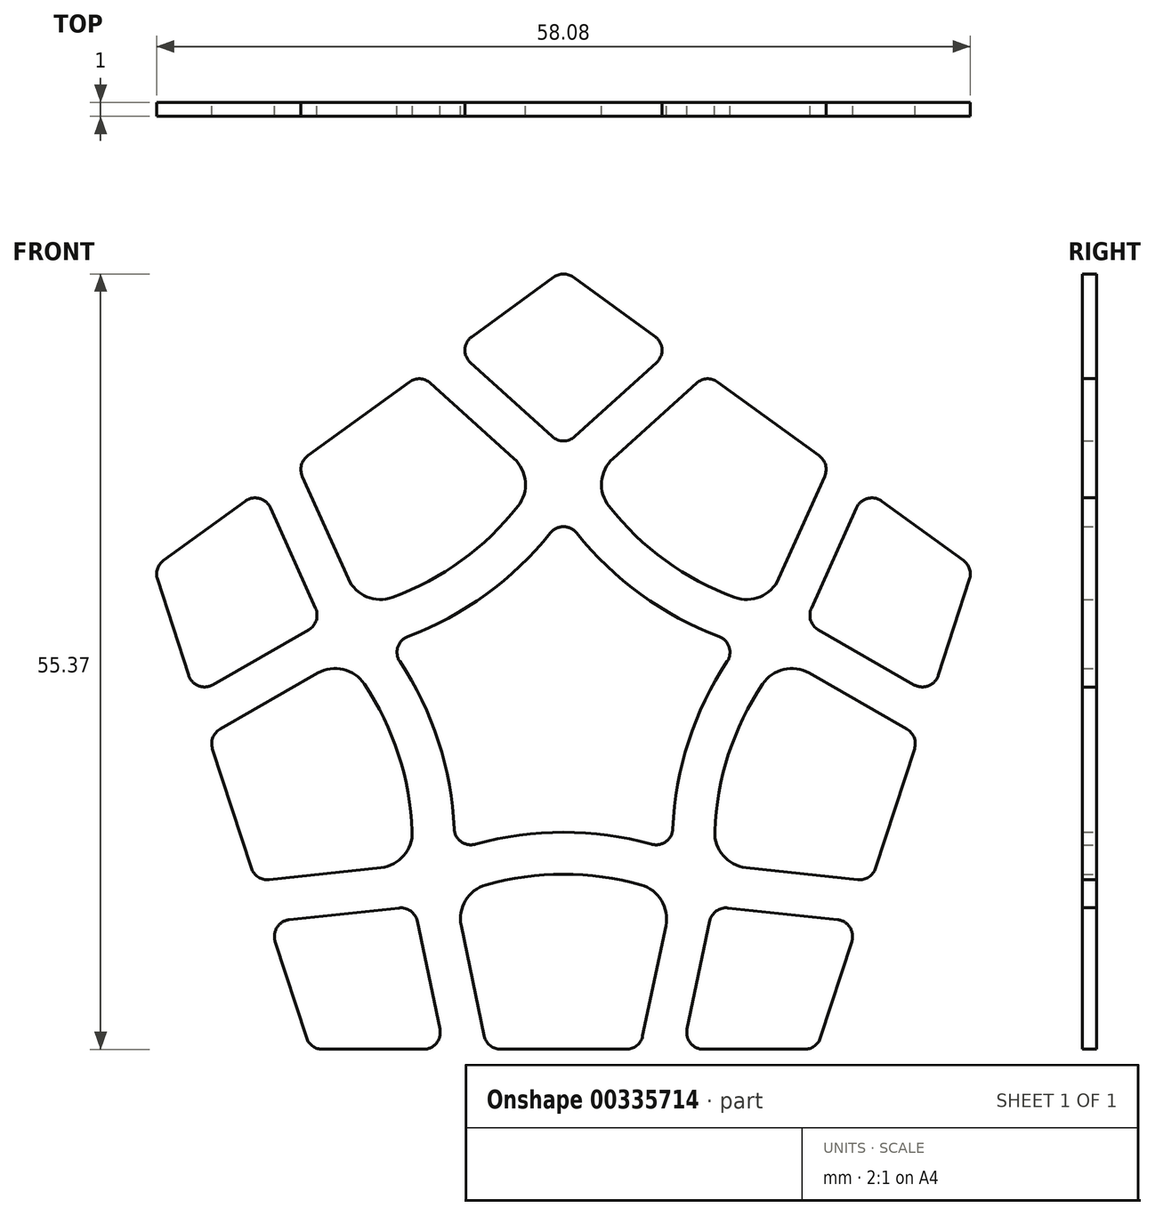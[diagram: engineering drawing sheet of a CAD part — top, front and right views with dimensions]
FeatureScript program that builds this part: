
annotation { "Feature Type Name" : "Feature", "Feature Type Description" : "" }
export const myFeature = defineFeature(function(context is Context, id is Id, definition is map)
    precondition{}
    {
        {
            var Q0;
            Q0=qCreatedBy(makeId("Front.planeOp"),FACE);
            var sketch = newSketch(context, id + "F0", { "sketchPlane" : qUnion([Q0])});
            skCircle(sketch, "E0.cCircle", {"center": v(0, 0) * mm, "radius": 26.39 * mm, "construction": true});
            skLineSegment(sketch, "E0.0", {"start": v(19.17, -26.39) * mm, "end": v(-19.17, -26.39) * mm});
            skLineSegment(sketch, "E0.1", {"start": v(-19.17, -26.39) * mm, "end": v(-31.02, 10.08) * mm});
            skLineSegment(sketch, "E0.2", {"start": v(-31.02, 10.08) * mm, "end": v(0, 32.61) * mm});
            skLineSegment(sketch, "E0.3", {"start": v(0, 32.61) * mm, "end": v(31.02, 10.08) * mm});
            skLineSegment(sketch, "E0.4", {"start": v(31.02, 10.08) * mm, "end": v(19.17, -26.39) * mm});
            skPoint(sketch, "E0.0.midPoint", {"position": v(0, -26.39) * mm});
            skArc(sketch, "E1", {"start": v(9.47, -13.04) * mm, "mid": v(0, -10.89) * mm, "end": v(-9.47, -13.04) * mm, "construction": true});
            skLineSegment(sketch, "E2", {"start": v(-19.57, -15.63) * mm, "end": v(-11.74, -14.79) * mm});
            skLineSegment(sketch, "E3", {"start": v(-10.44, -15.74) * mm, "end": v(-8.82, -23.44) * mm});
            skLineSegment(sketch, "E4", {"start": v(-10, -24.89) * mm, "end": v(-17.2, -24.89) * mm});
            skLineSegment(sketch, "E5", {"start": v(-18.35, -24.06) * mm, "end": v(-20.58, -17.2) * mm});
            skPoint(sketch, "E6.visualSharp", {"position": v(-21.04, -15.8) * mm});
            skArc(sketch, "E6.filletArc", {"start": v(-19.57, -15.63) * mm, "mid": v(-20.44, -16.17) * mm, "end": v(-20.58, -17.2) * mm});
            skPoint(sketch, "E7.visualSharp", {"position": v(-10.66, -14.67) * mm});
            skArc(sketch, "E7.filletArc", {"start": v(-10.44, -15.74) * mm, "mid": v(-10.9, -15.01) * mm, "end": v(-11.74, -14.79) * mm});
            skPoint(sketch, "E8.visualSharp", {"position": v(-8.52, -24.89) * mm});
            skArc(sketch, "E8.filletArc", {"start": v(-10, -24.89) * mm, "mid": v(-9.06, -24.44) * mm, "end": v(-8.82, -23.44) * mm});
            skPoint(sketch, "E9.visualSharp", {"position": v(-18.08, -24.89) * mm});
            skArc(sketch, "E9.filletArc", {"start": v(-18.35, -24.06) * mm, "mid": v(-17.91, -24.66) * mm, "end": v(-17.2, -24.89) * mm});
            skLineSegment(sketch, "E10", {"start": v(-7.3, -16.07) * mm, "end": v(-5.65, -23.93) * mm});
            skLineSegment(sketch, "E11", {"start": v(-4.48, -24.89) * mm, "end": v(4.48, -24.89) * mm});
            skLineSegment(sketch, "E12", {"start": v(5.65, -23.93) * mm, "end": v(7.3, -16.07) * mm});
            skArc(sketch, "E13", {"start": v(5.53, -13.15) * mm, "mid": v(0, -12.39) * mm, "end": v(-5.53, -13.15) * mm});
            skPoint(sketch, "E14.visualSharp", {"position": v(-5.45, -24.89) * mm});
            skArc(sketch, "E14.filletArc", {"start": v(-5.65, -23.93) * mm, "mid": v(-5.23, -24.62) * mm, "end": v(-4.48, -24.89) * mm});
            skPoint(sketch, "E15.visualSharp", {"position": v(5.45, -24.89) * mm});
            skArc(sketch, "E15.filletArc", {"start": v(4.48, -24.89) * mm, "mid": v(5.23, -24.62) * mm, "end": v(5.65, -23.93) * mm});
            skPoint(sketch, "E16.visualSharp", {"position": v(-7.75, -13.91) * mm});
            skArc(sketch, "E16.filletArc", {"start": v(-5.53, -13.15) * mm, "mid": v(-7, -14.26) * mm, "end": v(-7.3, -16.07) * mm});
            skPoint(sketch, "E17.visualSharp", {"position": v(7.75, -13.91) * mm});
            skArc(sketch, "E17.filletArc", {"start": v(7.3, -16.07) * mm, "mid": v(7, -14.26) * mm, "end": v(5.53, -13.15) * mm});
            skLineSegment(sketch, "E18.1.0", {"start": v(8.82, -23.44) * mm, "end": v(10.44, -15.74) * mm});
            skArc(sketch, "E18.1.1", {"start": v(8.82, -23.44) * mm, "mid": v(9.06, -24.44) * mm, "end": v(10, -24.89) * mm});
            skLineSegment(sketch, "E18.1.2", {"start": v(17.2, -24.89) * mm, "end": v(10, -24.89) * mm});
            skArc(sketch, "E18.1.3", {"start": v(17.2, -24.89) * mm, "mid": v(17.91, -24.66) * mm, "end": v(18.35, -24.06) * mm});
            skLineSegment(sketch, "E18.1.4", {"start": v(20.58, -17.2) * mm, "end": v(18.35, -24.06) * mm});
            skArc(sketch, "E18.1.5", {"start": v(20.58, -17.2) * mm, "mid": v(20.44, -16.17) * mm, "end": v(19.57, -15.63) * mm});
            skLineSegment(sketch, "E18.1.6", {"start": v(11.74, -14.79) * mm, "end": v(19.57, -15.63) * mm});
            skArc(sketch, "E18.1.7", {"start": v(11.74, -14.79) * mm, "mid": v(10.9, -15.01) * mm, "end": v(10.44, -15.74) * mm});
            skArc(sketch, "E18.1.8", {"start": v(10.8, -9.33) * mm, "mid": v(11.4, -11.06) * mm, "end": v(13.03, -11.91) * mm});
            skLineSegment(sketch, "E18.1.9", {"start": v(13.03, -11.91) * mm, "end": v(21.01, -12.77) * mm});
            skArc(sketch, "E18.1.10", {"start": v(21.01, -12.77) * mm, "mid": v(21.8, -12.59) * mm, "end": v(22.28, -11.95) * mm});
            skLineSegment(sketch, "E18.1.11", {"start": v(22.28, -11.95) * mm, "end": v(25.05, -3.43) * mm});
            skArc(sketch, "E18.1.12", {"start": v(25.05, -3.43) * mm, "mid": v(25.03, -2.63) * mm, "end": v(24.5, -2.02) * mm});
            skLineSegment(sketch, "E18.1.13", {"start": v(24.5, -2.02) * mm, "end": v(17.54, 1.98) * mm});
            skArc(sketch, "E18.1.14", {"start": v(17.54, 1.98) * mm, "mid": v(15.72, 2.25) * mm, "end": v(14.22, 1.2) * mm});
            skArc(sketch, "E18.1.15", {"start": v(14.22, 1.2) * mm, "mid": v(11.78, -3.83) * mm, "end": v(10.8, -9.33) * mm});
            skLineSegment(sketch, "E18.2.0", {"start": v(25.02, 1.15) * mm, "end": v(18.2, 5.06) * mm});
            skArc(sketch, "E18.2.1", {"start": v(25.02, 1.15) * mm, "mid": v(26.05, 1.07) * mm, "end": v(26.76, 1.82) * mm});
            skLineSegment(sketch, "E18.2.2", {"start": v(28.99, 8.68) * mm, "end": v(26.76, 1.82) * mm});
            skArc(sketch, "E18.2.3", {"start": v(28.99, 8.68) * mm, "mid": v(28.99, 9.42) * mm, "end": v(28.55, 10.02) * mm});
            skLineSegment(sketch, "E18.2.4", {"start": v(22.71, 14.26) * mm, "end": v(28.55, 10.02) * mm});
            skArc(sketch, "E18.2.5", {"start": v(22.71, 14.26) * mm, "mid": v(21.7, 14.45) * mm, "end": v(20.91, 13.78) * mm});
            skLineSegment(sketch, "E18.2.6", {"start": v(17.7, 6.6) * mm, "end": v(20.91, 13.78) * mm});
            skArc(sketch, "E18.2.7", {"start": v(17.7, 6.6) * mm, "mid": v(17.65, 5.73) * mm, "end": v(18.2, 5.06) * mm});
            skArc(sketch, "E18.2.8", {"start": v(12.2, 7.39) * mm, "mid": v(14.04, 7.43) * mm, "end": v(15.35, 8.7) * mm});
            skLineSegment(sketch, "E18.2.9", {"start": v(15.35, 8.7) * mm, "end": v(18.64, 16.04) * mm});
            skArc(sketch, "E18.2.10", {"start": v(18.64, 16.04) * mm, "mid": v(18.7, 16.84) * mm, "end": v(18.25, 17.5) * mm});
            skLineSegment(sketch, "E18.2.11", {"start": v(18.25, 17.5) * mm, "end": v(11, 22.77) * mm});
            skArc(sketch, "E18.2.12", {"start": v(11, 22.77) * mm, "mid": v(10.23, 23) * mm, "end": v(9.5, 22.68) * mm});
            skLineSegment(sketch, "E18.2.13", {"start": v(9.5, 22.68) * mm, "end": v(3.54, 17.3) * mm});
            skArc(sketch, "E18.2.14", {"start": v(3.54, 17.3) * mm, "mid": v(2.72, 15.65) * mm, "end": v(3.25, 13.9) * mm});
            skArc(sketch, "E18.2.15", {"start": v(3.25, 13.9) * mm, "mid": v(7.28, 10.02) * mm, "end": v(12.2, 7.39) * mm});
            skLineSegment(sketch, "E18.3.0", {"start": v(6.64, 24.15) * mm, "end": v(0.8, 18.87) * mm});
            skArc(sketch, "E18.3.1", {"start": v(6.64, 24.15) * mm, "mid": v(7.03, 25.1) * mm, "end": v(6.54, 26) * mm});
            skLineSegment(sketch, "E18.3.2", {"start": v(0.7, 30.25) * mm, "end": v(6.54, 26) * mm});
            skArc(sketch, "E18.3.3", {"start": v(0.7, 30.25) * mm, "mid": v(0, 30.48) * mm, "end": v(-0.7, 30.25) * mm});
            skLineSegment(sketch, "E18.3.4", {"start": v(-6.54, 26) * mm, "end": v(-0.7, 30.25) * mm});
            skArc(sketch, "E18.3.5", {"start": v(-6.54, 26) * mm, "mid": v(-7.03, 25.1) * mm, "end": v(-6.64, 24.15) * mm});
            skLineSegment(sketch, "E18.3.6", {"start": v(-0.8, 18.87) * mm, "end": v(-6.64, 24.15) * mm});
            skArc(sketch, "E18.3.7", {"start": v(-0.8, 18.87) * mm, "mid": v(0, 18.56) * mm, "end": v(0.8, 18.87) * mm});
            skArc(sketch, "E18.3.8", {"start": v(-3.25, 13.9) * mm, "mid": v(-2.72, 15.65) * mm, "end": v(-3.54, 17.3) * mm});
            skLineSegment(sketch, "E18.3.9", {"start": v(-3.54, 17.3) * mm, "end": v(-9.5, 22.68) * mm});
            skArc(sketch, "E18.3.10", {"start": v(-9.5, 22.68) * mm, "mid": v(-10.23, 23) * mm, "end": v(-11, 22.77) * mm});
            skLineSegment(sketch, "E18.3.11", {"start": v(-11, 22.77) * mm, "end": v(-18.25, 17.5) * mm});
            skArc(sketch, "E18.3.12", {"start": v(-18.25, 17.5) * mm, "mid": v(-18.7, 16.84) * mm, "end": v(-18.64, 16.04) * mm});
            skLineSegment(sketch, "E18.3.13", {"start": v(-18.64, 16.04) * mm, "end": v(-15.35, 8.7) * mm});
            skArc(sketch, "E18.3.14", {"start": v(-15.35, 8.7) * mm, "mid": v(-14.04, 7.43) * mm, "end": v(-12.2, 7.39) * mm});
            skArc(sketch, "E18.3.15", {"start": v(-12.2, 7.39) * mm, "mid": v(-7.28, 10.02) * mm, "end": v(-3.25, 13.9) * mm});
            skLineSegment(sketch, "E18.4.0", {"start": v(-20.91, 13.78) * mm, "end": v(-17.7, 6.6) * mm});
            skArc(sketch, "E18.4.1", {"start": v(-20.91, 13.78) * mm, "mid": v(-21.7, 14.45) * mm, "end": v(-22.71, 14.26) * mm});
            skLineSegment(sketch, "E18.4.2", {"start": v(-28.55, 10.02) * mm, "end": v(-22.71, 14.26) * mm});
            skArc(sketch, "E18.4.3", {"start": v(-28.55, 10.02) * mm, "mid": v(-28.99, 9.42) * mm, "end": v(-28.99, 8.68) * mm});
            skLineSegment(sketch, "E18.4.4", {"start": v(-26.76, 1.82) * mm, "end": v(-28.99, 8.68) * mm});
            skArc(sketch, "E18.4.5", {"start": v(-26.76, 1.82) * mm, "mid": v(-26.05, 1.07) * mm, "end": v(-25.02, 1.15) * mm});
            skLineSegment(sketch, "E18.4.6", {"start": v(-18.2, 5.06) * mm, "end": v(-25.02, 1.15) * mm});
            skArc(sketch, "E18.4.7", {"start": v(-18.2, 5.06) * mm, "mid": v(-17.65, 5.73) * mm, "end": v(-17.7, 6.6) * mm});
            skArc(sketch, "E18.4.8", {"start": v(-14.22, 1.2) * mm, "mid": v(-15.72, 2.25) * mm, "end": v(-17.54, 1.98) * mm});
            skLineSegment(sketch, "E18.4.9", {"start": v(-17.54, 1.98) * mm, "end": v(-24.5, -2.02) * mm});
            skArc(sketch, "E18.4.10", {"start": v(-24.5, -2.02) * mm, "mid": v(-25.03, -2.63) * mm, "end": v(-25.05, -3.43) * mm});
            skLineSegment(sketch, "E18.4.11", {"start": v(-25.05, -3.43) * mm, "end": v(-22.28, -11.95) * mm});
            skArc(sketch, "E18.4.12", {"start": v(-22.28, -11.95) * mm, "mid": v(-21.8, -12.59) * mm, "end": v(-21.01, -12.77) * mm});
            skLineSegment(sketch, "E18.4.13", {"start": v(-21.01, -12.77) * mm, "end": v(-13.03, -11.91) * mm});
            skArc(sketch, "E18.4.14", {"start": v(-13.03, -11.91) * mm, "mid": v(-11.4, -11.06) * mm, "end": v(-10.8, -9.33) * mm});
            skArc(sketch, "E18.4.15", {"start": v(-10.8, -9.33) * mm, "mid": v(-11.78, -3.83) * mm, "end": v(-14.22, 1.2) * mm});
            skArc(sketch, "E19.4", {"start": v(6.28, -10.24) * mm, "mid": v(0, -9.39) * mm, "end": v(-6.28, -10.24) * mm});
            skLineSegment(sketch, "E20", {"start": v(-19.17, -26.39) * mm, "end": v(0, 0) * mm, "construction": true});
            skLineSegment(sketch, "E21", {"start": v(0, -26.39) * mm, "end": v(0, 0) * mm, "construction": true});
            skLineSegment(sketch, "E22", {"start": v(19.17, -26.39) * mm, "end": v(0, 0) * mm, "construction": true});
            skLineSegment(sketch, "E23", {"start": v(-9.47, -13.04) * mm, "end": v(9.47, -13.04) * mm, "construction": true});
            skLineSegment(sketch, "E24", {"start": v(-9.47, -13.04) * mm, "end": v(-6.67, -26.39) * mm, "construction": true});
            skLineSegment(sketch, "E25", {"start": v(-9.47, -13.04) * mm, "end": v(-23.03, -14.5) * mm, "construction": true});
            skLineSegment(sketch, "E26", {"start": v(9.47, -13.04) * mm, "end": v(6.67, -26.39) * mm, "construction": true});
            skArc(sketch, "E27.1.0", {"start": v(11.68, 2.8) * mm, "mid": v(8.93, -2.9) * mm, "end": v(7.8, -9.14) * mm});
            skArc(sketch, "E27.2.0", {"start": v(0.94, 11.98) * mm, "mid": v(5.52, 7.6) * mm, "end": v(11.1, 4.6) * mm});
            skArc(sketch, "E27.3.0", {"start": v(-11.1, 4.6) * mm, "mid": v(-5.52, 7.6) * mm, "end": v(-0.94, 11.98) * mm});
            skArc(sketch, "E27.4.0", {"start": v(-7.8, -9.14) * mm, "mid": v(-8.93, -2.9) * mm, "end": v(-11.68, 2.8) * mm});
            skPoint(sketch, "E28.visualSharp", {"position": v(-12.6, 4.1) * mm});
            skArc(sketch, "E28.filletArc", {"start": v(-11.1, 4.6) * mm, "mid": v(-11.82, 3.84) * mm, "end": v(-11.68, 2.8) * mm});
            skPoint(sketch, "E29.visualSharp", {"position": v(0, 13.25) * mm});
            skArc(sketch, "E29.filletArc", {"start": v(0.94, 11.98) * mm, "mid": v(0, 12.43) * mm, "end": v(-0.94, 11.98) * mm});
            skPoint(sketch, "E30.visualSharp", {"position": v(12.6, 4.1) * mm});
            skArc(sketch, "E30.filletArc", {"start": v(11.68, 2.8) * mm, "mid": v(11.82, 3.84) * mm, "end": v(11.1, 4.6) * mm});
            skArc(sketch, "E31.filletArc", {"start": v(6.28, -10.24) * mm, "mid": v(7.3, -10.06) * mm, "end": v(7.8, -9.14) * mm});
            skArc(sketch, "E32.filletArc", {"start": v(-7.8, -9.14) * mm, "mid": v(-7.3, -10.06) * mm, "end": v(-6.28, -10.24) * mm});
            skSolve(sketch);
        }
        {
            var Q0;
            Q0=makeQuery(id+"F0.imprint","IMPRINT",FACE,{"disambiguationData":[TD([[makeQuery(id+"F0.imprint","IMPRINT",EDGE,{"derivedFrom":sQuery(id+"F0.wireOp",EDGE,"E18.4.0")}),-1.0]])]});
            var Q1;
            Q1=makeQuery(id+"F0.imprint","IMPRINT",FACE,{"disambiguationData":[TD([[makeQuery(id+"F0.imprint","IMPRINT",EDGE,{"derivedFrom":sQuery(id+"F0.wireOp",EDGE,"E18.3.8")}),1.0]])]});
            var Q2;
            Q2=makeQuery(id+"F0.imprint","IMPRINT",FACE,{"disambiguationData":[TD([[makeQuery(id+"F0.imprint","IMPRINT",EDGE,{"derivedFrom":sQuery(id+"F0.wireOp",EDGE,"E18.3.0")}),-1.0]])]});
            var Q3;
            Q3=makeQuery(id+"F0.imprint","IMPRINT",FACE,{"disambiguationData":[TD([[makeQuery(id+"F0.imprint","IMPRINT",EDGE,{"derivedFrom":sQuery(id+"F0.wireOp",EDGE,"E18.2.8")}),1.0]])]});
            var Q4;
            Q4=makeQuery(id+"F0.imprint","IMPRINT",FACE,{"disambiguationData":[TD([[makeQuery(id+"F0.imprint","IMPRINT",EDGE,{"derivedFrom":sQuery(id+"F0.wireOp",EDGE,"E19.0")}),-1.0]])]});
            var Q5;
            Q5=makeQuery(id+"F0.imprint","IMPRINT",FACE,{"disambiguationData":[TD([[makeQuery(id+"F0.imprint","IMPRINT",EDGE,{"derivedFrom":sQuery(id+"F0.wireOp",EDGE,"E18.4.8")}),1.0]])]});
            var Q6;
            Q6=makeQuery(id+"F0.imprint","IMPRINT",FACE,{"disambiguationData":[TD([[makeQuery(id+"F0.imprint","IMPRINT",EDGE,{"derivedFrom":sQuery(id+"F0.wireOp",EDGE,"E2")}),-1.0]])]});
            var Q7;
            Q7=makeQuery(id+"F0.imprint","IMPRINT",FACE,{"disambiguationData":[TD([[makeQuery(id+"F0.imprint","IMPRINT",EDGE,{"derivedFrom":sQuery(id+"F0.wireOp",EDGE,"E10")}),1.0]])]});
            var Q8;
            Q8=makeQuery(id+"F0.imprint","IMPRINT",FACE,{"disambiguationData":[TD([[makeQuery(id+"F0.imprint","IMPRINT",EDGE,{"derivedFrom":sQuery(id+"F0.wireOp",EDGE,"E18.1.0")}),-1.0]])]});
            var Q9;
            Q9=makeQuery(id+"F0.imprint","IMPRINT",FACE,{"disambiguationData":[TD([[makeQuery(id+"F0.imprint","IMPRINT",EDGE,{"derivedFrom":sQuery(id+"F0.wireOp",EDGE,"E18.1.8")}),1.0]])]});
            var Q10;
            Q10=makeQuery(id+"F0.imprint","IMPRINT",FACE,{"disambiguationData":[TD([[makeQuery(id+"F0.imprint","IMPRINT",EDGE,{"derivedFrom":sQuery(id+"F0.wireOp",EDGE,"E18.2.0")}),-1.0]])]});
            var Q11;
            Q11=makeQuery(id+"F0.imprint","IMPRINT",FACE,{"disambiguationData":[TD([[makeQuery(id+"F0.imprint","IMPRINT",EDGE,{"derivedFrom":sQuery(id+"F0.wireOp",EDGE,"E19.4")}),-1.0]])]});
            extrude(context, id + "F1", {"entities" : qUnion([Q0, Q1, Q2, Q3, Q4, Q5, Q6, Q7, Q8, Q9, Q10, Q11]), "depth" : 1 * mm});
        }
    });
